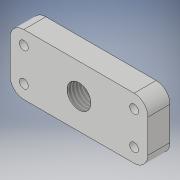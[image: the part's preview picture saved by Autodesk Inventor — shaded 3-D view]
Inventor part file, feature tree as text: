
AUTODESK INVENTOR PART (.ipt)
format: ipt  version: 2019.4 (Build 234330000, 330)  size: 126,976 bytes
history: native  units: mm
features: sketch x2, other x1, extrude x1, hole x1, fillet x1
ambient origin geometry x8: Origin, YZ Plane, XZ Plane, XY Plane, X Axis, Y Axis, Z Axis, Center Point
bodies: Body1 (feature_tree)
feature tree (6):
  other  "ソリッド1"
  extrude  "押し出し1"  Depth=50.0mm
  hole  "穴1"  [1 undecoded]
  fillet  "フィレット1"  Radius=8.0mm
  sketch  "スケッチ1"
  sketch  "スケッチ2"
note: 1 required parameter value undecoded (feature->parameter linkage not recoverable at this tier; creation-order binding heuristic only, values carry confidence <= 0.55)
